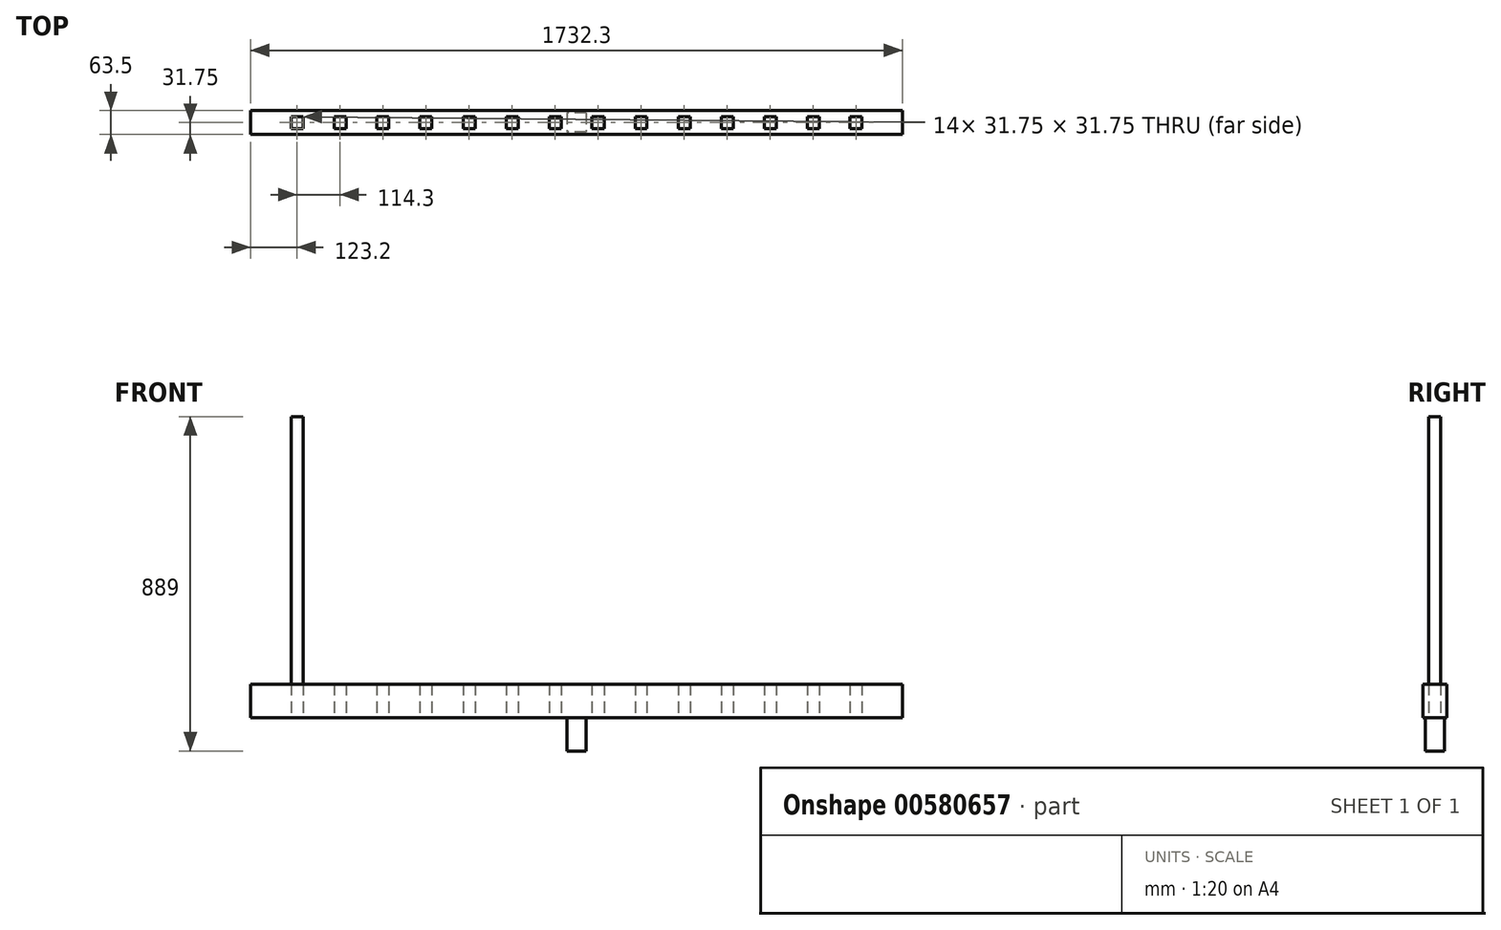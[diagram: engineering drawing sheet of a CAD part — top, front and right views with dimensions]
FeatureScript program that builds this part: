
annotation { "Feature Type Name" : "Feature", "Feature Type Description" : "" }
export const myFeature = defineFeature(function(context is Context, id is Id, definition is map)
    precondition{}
    {
        {
            var Q0;
            Q0=qCreatedBy(makeId("Top.planeOp"),FACE);
            var sketch = newSketch(context, id + "F0", { "sketchPlane" : qUnion([Q0])});
            skLineSegment(sketch, "E0.bottom", {"start": v(866.15, -31.75) * mm, "end": v(-866.15, -31.75) * mm});
            skLineSegment(sketch, "E0.top", {"start": v(866.15, 31.75) * mm, "end": v(-866.15, 31.75) * mm});
            skLineSegment(sketch, "E0.left", {"start": v(866.15, -31.75) * mm, "end": v(866.15, 31.75) * mm});
            skLineSegment(sketch, "E0.right", {"start": v(-866.15, -31.75) * mm, "end": v(-866.15, 31.75) * mm});
            skPoint(sketch, "E0.middle", {"position": v(0, 0) * mm});
            skLineSegment(sketch, "E1.bottom", {"start": v(-41.28, -15.88) * mm, "end": v(-73.03, -15.87) * mm});
            skLineSegment(sketch, "E1.top", {"start": v(-41.28, 15.87) * mm, "end": v(-73.03, 15.88) * mm});
            skLineSegment(sketch, "E1.left", {"start": v(-41.28, -15.87) * mm, "end": v(-41.28, 15.88) * mm});
            skLineSegment(sketch, "E1.right", {"start": v(-73.03, -15.87) * mm, "end": v(-73.03, 15.88) * mm});
            skPoint(sketch, "E1.middle", {"position": v(-57.15, 0) * mm});
            skLineSegment(sketch, "E2.bottom", {"start": v(-155.57, -15.87) * mm, "end": v(-187.32, -15.87) * mm});
            skLineSegment(sketch, "E2.top", {"start": v(-155.58, 15.88) * mm, "end": v(-187.33, 15.88) * mm});
            skLineSegment(sketch, "E2.left", {"start": v(-155.58, -15.87) * mm, "end": v(-155.58, 15.88) * mm});
            skLineSegment(sketch, "E2.right", {"start": v(-187.32, -15.87) * mm, "end": v(-187.32, 15.88) * mm});
            skPoint(sketch, "E2.middle", {"position": v(-171.45, 0) * mm});
            skLineSegment(sketch, "E3.bottom", {"start": v(-269.88, -15.87) * mm, "end": v(-301.63, -15.87) * mm});
            skLineSegment(sketch, "E3.top", {"start": v(-269.88, 15.88) * mm, "end": v(-301.63, 15.88) * mm});
            skLineSegment(sketch, "E3.left", {"start": v(-269.88, -15.87) * mm, "end": v(-269.88, 15.88) * mm});
            skLineSegment(sketch, "E3.right", {"start": v(-301.63, -15.87) * mm, "end": v(-301.63, 15.88) * mm});
            skPoint(sketch, "E3.middle", {"position": v(-285.75, 0) * mm});
            skPoint(sketch, "E3.cornerSnap0", {"position": v(-171.45, -15.87) * mm});
            skLineSegment(sketch, "E4.bottom", {"start": v(-384.18, -15.87) * mm, "end": v(-415.93, -15.87) * mm});
            skLineSegment(sketch, "E4.top", {"start": v(-384.18, 15.87) * mm, "end": v(-415.93, 15.87) * mm});
            skLineSegment(sketch, "E4.left", {"start": v(-384.18, -15.87) * mm, "end": v(-384.18, 15.87) * mm});
            skLineSegment(sketch, "E4.right", {"start": v(-415.93, -15.87) * mm, "end": v(-415.93, 15.87) * mm});
            skPoint(sketch, "E4.middle", {"position": v(-400.05, 0) * mm});
            skPoint(sketch, "E4.cornerSnap0", {"position": v(-285.75, -15.87) * mm});
            skLineSegment(sketch, "E5.bottom", {"start": v(-498.48, -15.87) * mm, "end": v(-530.23, -15.87) * mm});
            skLineSegment(sketch, "E5.top", {"start": v(-498.48, 15.88) * mm, "end": v(-530.23, 15.88) * mm});
            skLineSegment(sketch, "E5.left", {"start": v(-498.48, -15.87) * mm, "end": v(-498.48, 15.87) * mm});
            skLineSegment(sketch, "E5.right", {"start": v(-530.23, -15.88) * mm, "end": v(-530.23, 15.88) * mm});
            skPoint(sketch, "E5.middle", {"position": v(-514.35, 0) * mm});
            skPoint(sketch, "E5.middle.positionSnap0", {"position": v(-415.93, 0) * mm});
            skPoint(sketch, "E5.centerSnap0", {"position": v(-415.93, 0) * mm});
            skLineSegment(sketch, "E6.bottom", {"start": v(-612.77, -15.87) * mm, "end": v(-644.52, -15.87) * mm});
            skLineSegment(sketch, "E6.top", {"start": v(-612.77, 15.88) * mm, "end": v(-644.52, 15.88) * mm});
            skLineSegment(sketch, "E6.left", {"start": v(-612.77, -15.88) * mm, "end": v(-612.77, 15.88) * mm});
            skLineSegment(sketch, "E6.right", {"start": v(-644.52, -15.88) * mm, "end": v(-644.52, 15.87) * mm});
            skPoint(sketch, "E6.middle", {"position": v(-628.65, 0) * mm});
            skLineSegment(sketch, "E7.bottom", {"start": v(-727.07, -15.88) * mm, "end": v(-758.82, -15.88) * mm});
            skLineSegment(sketch, "E7.top", {"start": v(-727.07, 15.87) * mm, "end": v(-758.82, 15.87) * mm});
            skLineSegment(sketch, "E7.left", {"start": v(-727.07, -15.88) * mm, "end": v(-727.07, 15.87) * mm});
            skLineSegment(sketch, "E7.right", {"start": v(-758.82, -15.88) * mm, "end": v(-758.82, 15.87) * mm});
            skPoint(sketch, "E7.middle", {"position": v(-742.95, 0) * mm});
            skLineSegment(sketch, "E8.bottom", {"start": v(73.03, -15.88) * mm, "end": v(41.27, -15.88) * mm});
            skLineSegment(sketch, "E8.top", {"start": v(73.03, 15.87) * mm, "end": v(41.28, 15.87) * mm});
            skLineSegment(sketch, "E8.left", {"start": v(73.03, -15.88) * mm, "end": v(73.03, 15.87) * mm});
            skLineSegment(sketch, "E8.right", {"start": v(41.28, -15.88) * mm, "end": v(41.28, 15.87) * mm});
            skPoint(sketch, "E8.middle", {"position": v(57.15, 0) * mm});
            skLineSegment(sketch, "E9.bottom", {"start": v(187.33, -15.88) * mm, "end": v(155.58, -15.88) * mm});
            skLineSegment(sketch, "E9.top", {"start": v(187.33, 15.87) * mm, "end": v(155.58, 15.87) * mm});
            skLineSegment(sketch, "E9.left", {"start": v(187.33, -15.88) * mm, "end": v(187.33, 15.87) * mm});
            skLineSegment(sketch, "E9.right", {"start": v(155.58, -15.88) * mm, "end": v(155.58, 15.87) * mm});
            skPoint(sketch, "E9.middle", {"position": v(171.45, 0) * mm});
            skLineSegment(sketch, "E10.bottom", {"start": v(301.63, -15.88) * mm, "end": v(269.88, -15.88) * mm});
            skLineSegment(sketch, "E10.top", {"start": v(301.63, 15.87) * mm, "end": v(269.88, 15.87) * mm});
            skLineSegment(sketch, "E10.left", {"start": v(301.63, -15.88) * mm, "end": v(301.63, 15.87) * mm});
            skLineSegment(sketch, "E10.right", {"start": v(269.88, -15.88) * mm, "end": v(269.88, 15.87) * mm});
            skPoint(sketch, "E10.middle", {"position": v(285.75, 0) * mm});
            skLineSegment(sketch, "E11.bottom", {"start": v(415.93, -15.88) * mm, "end": v(384.18, -15.88) * mm});
            skLineSegment(sketch, "E11.top", {"start": v(415.93, 15.87) * mm, "end": v(384.18, 15.87) * mm});
            skLineSegment(sketch, "E11.left", {"start": v(415.93, -15.88) * mm, "end": v(415.93, 15.87) * mm});
            skLineSegment(sketch, "E11.right", {"start": v(384.18, -15.88) * mm, "end": v(384.18, 15.87) * mm});
            skPoint(sketch, "E11.middle", {"position": v(400.05, 0) * mm});
            skLineSegment(sketch, "E12.bottom", {"start": v(530.23, -15.88) * mm, "end": v(498.48, -15.88) * mm});
            skLineSegment(sketch, "E12.top", {"start": v(530.23, 15.87) * mm, "end": v(498.48, 15.87) * mm});
            skLineSegment(sketch, "E12.left", {"start": v(530.23, -15.88) * mm, "end": v(530.23, 15.87) * mm});
            skLineSegment(sketch, "E12.right", {"start": v(498.48, -15.88) * mm, "end": v(498.48, 15.87) * mm});
            skPoint(sketch, "E12.middle", {"position": v(514.35, 0) * mm});
            skLineSegment(sketch, "E13.bottom", {"start": v(644.53, -15.88) * mm, "end": v(612.78, -15.88) * mm});
            skLineSegment(sketch, "E13.top", {"start": v(644.53, 15.87) * mm, "end": v(612.78, 15.87) * mm});
            skLineSegment(sketch, "E13.left", {"start": v(644.53, -15.88) * mm, "end": v(644.53, 15.87) * mm});
            skLineSegment(sketch, "E13.right", {"start": v(612.78, -15.88) * mm, "end": v(612.78, 15.87) * mm});
            skPoint(sketch, "E13.middle", {"position": v(628.65, 0) * mm});
            skLineSegment(sketch, "E14.bottom", {"start": v(758.82, -15.88) * mm, "end": v(727.07, -15.88) * mm});
            skLineSegment(sketch, "E14.top", {"start": v(758.82, 15.87) * mm, "end": v(727.07, 15.87) * mm});
            skLineSegment(sketch, "E14.left", {"start": v(758.82, -15.88) * mm, "end": v(758.82, 15.87) * mm});
            skLineSegment(sketch, "E14.right", {"start": v(727.07, -15.88) * mm, "end": v(727.07, 15.87) * mm});
            skPoint(sketch, "E14.middle", {"position": v(742.95, 0) * mm});
            skSolve(sketch);
        }
        {
            var Q0;
            Q0=makeQuery(id+"F0.imprint","IMPRINT",FACE,{"disambiguationData":[TD([[makeQuery(id+"F0.imprint","IMPRINT",EDGE,{"derivedFrom":sQuery(id+"F0.wireOp",EDGE,"E0.bottom")}),-1.0]])]});
            extrude(context, id + "F1", {"entities" : qUnion([Q0]), "depth" : 88.9 * mm, "offsetDistance" : 25.4 * mm});
        }
        {
            var Q0;
            Q0=makeQuery(id+"F1.opExtrude","CAP_FACE",FACE,{"disambiguationData":[OSD([sQuery(id+"F0.wireOp",EDGE,"E0.bottom"),sQuery(id+"F0.wireOp",EDGE,"E0.top"),sQuery(id+"F0.wireOp",EDGE,"E0.left"),sQuery(id+"F0.wireOp",EDGE,"E0.right"),sQuery(id+"F0.wireOp",EDGE,"E1.bottom"),sQuery(id+"F0.wireOp",EDGE,"E1.top"),sQuery(id+"F0.wireOp",EDGE,"E1.left"),sQuery(id+"F0.wireOp",EDGE,"E1.right"),sQuery(id+"F0.wireOp",EDGE,"E2.bottom"),sQuery(id+"F0.wireOp",EDGE,"E2.top"),sQuery(id+"F0.wireOp",EDGE,"E2.left"),sQuery(id+"F0.wireOp",EDGE,"E2.right"),sQuery(id+"F0.wireOp",EDGE,"E3.bottom"),sQuery(id+"F0.wireOp",EDGE,"E3.top"),sQuery(id+"F0.wireOp",EDGE,"E3.left"),sQuery(id+"F0.wireOp",EDGE,"E3.right"),sQuery(id+"F0.wireOp",EDGE,"E4.bottom"),sQuery(id+"F0.wireOp",EDGE,"E4.top"),sQuery(id+"F0.wireOp",EDGE,"E4.left"),sQuery(id+"F0.wireOp",EDGE,"E4.right"),sQuery(id+"F0.wireOp",EDGE,"E5.bottom"),sQuery(id+"F0.wireOp",EDGE,"E5.top"),sQuery(id+"F0.wireOp",EDGE,"E5.left"),sQuery(id+"F0.wireOp",EDGE,"E5.right"),sQuery(id+"F0.wireOp",EDGE,"E6.bottom"),sQuery(id+"F0.wireOp",EDGE,"E6.top"),sQuery(id+"F0.wireOp",EDGE,"E6.left"),sQuery(id+"F0.wireOp",EDGE,"E6.right"),sQuery(id+"F0.wireOp",EDGE,"E7.bottom"),sQuery(id+"F0.wireOp",EDGE,"E7.top"),sQuery(id+"F0.wireOp",EDGE,"E7.left"),sQuery(id+"F0.wireOp",EDGE,"E7.right"),sQuery(id+"F0.wireOp",EDGE,"E8.bottom"),sQuery(id+"F0.wireOp",EDGE,"E8.top"),sQuery(id+"F0.wireOp",EDGE,"E8.left"),sQuery(id+"F0.wireOp",EDGE,"E8.right"),sQuery(id+"F0.wireOp",EDGE,"E9.bottom"),sQuery(id+"F0.wireOp",EDGE,"E9.top"),sQuery(id+"F0.wireOp",EDGE,"E9.left"),sQuery(id+"F0.wireOp",EDGE,"E9.right"),sQuery(id+"F0.wireOp",EDGE,"E10.bottom"),sQuery(id+"F0.wireOp",EDGE,"E10.top"),sQuery(id+"F0.wireOp",EDGE,"E10.left"),sQuery(id+"F0.wireOp",EDGE,"E10.right"),sQuery(id+"F0.wireOp",EDGE,"E11.bottom"),sQuery(id+"F0.wireOp",EDGE,"E11.top"),sQuery(id+"F0.wireOp",EDGE,"E11.left"),sQuery(id+"F0.wireOp",EDGE,"E11.right"),sQuery(id+"F0.wireOp",EDGE,"E12.bottom"),sQuery(id+"F0.wireOp",EDGE,"E12.top"),sQuery(id+"F0.wireOp",EDGE,"E12.left"),sQuery(id+"F0.wireOp",EDGE,"E12.right"),sQuery(id+"F0.wireOp",EDGE,"E13.bottom"),sQuery(id+"F0.wireOp",EDGE,"E13.top"),sQuery(id+"F0.wireOp",EDGE,"E13.left"),sQuery(id+"F0.wireOp",EDGE,"E13.right"),sQuery(id+"F0.wireOp",EDGE,"E14.bottom"),sQuery(id+"F0.wireOp",EDGE,"E14.top"),sQuery(id+"F0.wireOp",EDGE,"E14.left"),sQuery(id+"F0.wireOp",EDGE,"E14.right")])],"isStart":false});
            var sketch = newSketch(context, id + "F2", { "sketchPlane" : qUnion([Q0])});
            skLineSegment(sketch, "E15.bottom", {"start": v(-758.82, 15.87) * mm, "end": v(-727.07, 15.87) * mm});
            skLineSegment(sketch, "E15.top", {"start": v(-758.82, -15.88) * mm, "end": v(-727.07, -15.88) * mm});
            skLineSegment(sketch, "E15.left", {"start": v(-758.82, 15.87) * mm, "end": v(-758.82, -15.88) * mm});
            skLineSegment(sketch, "E15.right", {"start": v(-727.07, 15.87) * mm, "end": v(-727.07, -15.88) * mm});
            skSolve(sketch);
        }
        {
            var Q0;
            Q0=makeQuery(id+"F1.opExtrude","CAP_FACE",FACE,{"disambiguationData":[OSD([sQuery(id+"F0.wireOp",EDGE,"E0.bottom"),sQuery(id+"F0.wireOp",EDGE,"E0.top"),sQuery(id+"F0.wireOp",EDGE,"E0.left"),sQuery(id+"F0.wireOp",EDGE,"E0.right"),sQuery(id+"F0.wireOp",EDGE,"E1.bottom"),sQuery(id+"F0.wireOp",EDGE,"E1.top"),sQuery(id+"F0.wireOp",EDGE,"E1.left"),sQuery(id+"F0.wireOp",EDGE,"E1.right"),sQuery(id+"F0.wireOp",EDGE,"E2.bottom"),sQuery(id+"F0.wireOp",EDGE,"E2.top"),sQuery(id+"F0.wireOp",EDGE,"E2.left"),sQuery(id+"F0.wireOp",EDGE,"E2.right"),sQuery(id+"F0.wireOp",EDGE,"E3.bottom"),sQuery(id+"F0.wireOp",EDGE,"E3.top"),sQuery(id+"F0.wireOp",EDGE,"E3.left"),sQuery(id+"F0.wireOp",EDGE,"E3.right"),sQuery(id+"F0.wireOp",EDGE,"E4.bottom"),sQuery(id+"F0.wireOp",EDGE,"E4.top"),sQuery(id+"F0.wireOp",EDGE,"E4.left"),sQuery(id+"F0.wireOp",EDGE,"E4.right"),sQuery(id+"F0.wireOp",EDGE,"E5.bottom"),sQuery(id+"F0.wireOp",EDGE,"E5.top"),sQuery(id+"F0.wireOp",EDGE,"E5.left"),sQuery(id+"F0.wireOp",EDGE,"E5.right"),sQuery(id+"F0.wireOp",EDGE,"E6.bottom"),sQuery(id+"F0.wireOp",EDGE,"E6.top"),sQuery(id+"F0.wireOp",EDGE,"E6.left"),sQuery(id+"F0.wireOp",EDGE,"E6.right"),sQuery(id+"F0.wireOp",EDGE,"E7.bottom"),sQuery(id+"F0.wireOp",EDGE,"E7.top"),sQuery(id+"F0.wireOp",EDGE,"E7.left"),sQuery(id+"F0.wireOp",EDGE,"E7.right"),sQuery(id+"F0.wireOp",EDGE,"E8.bottom"),sQuery(id+"F0.wireOp",EDGE,"E8.top"),sQuery(id+"F0.wireOp",EDGE,"E8.left"),sQuery(id+"F0.wireOp",EDGE,"E8.right"),sQuery(id+"F0.wireOp",EDGE,"E9.bottom"),sQuery(id+"F0.wireOp",EDGE,"E9.top"),sQuery(id+"F0.wireOp",EDGE,"E9.left"),sQuery(id+"F0.wireOp",EDGE,"E9.right"),sQuery(id+"F0.wireOp",EDGE,"E10.bottom"),sQuery(id+"F0.wireOp",EDGE,"E10.top"),sQuery(id+"F0.wireOp",EDGE,"E10.left"),sQuery(id+"F0.wireOp",EDGE,"E10.right"),sQuery(id+"F0.wireOp",EDGE,"E11.bottom"),sQuery(id+"F0.wireOp",EDGE,"E11.top"),sQuery(id+"F0.wireOp",EDGE,"E11.left"),sQuery(id+"F0.wireOp",EDGE,"E11.right"),sQuery(id+"F0.wireOp",EDGE,"E12.bottom"),sQuery(id+"F0.wireOp",EDGE,"E12.top"),sQuery(id+"F0.wireOp",EDGE,"E12.left"),sQuery(id+"F0.wireOp",EDGE,"E12.right"),sQuery(id+"F0.wireOp",EDGE,"E13.bottom"),sQuery(id+"F0.wireOp",EDGE,"E13.top"),sQuery(id+"F0.wireOp",EDGE,"E13.left"),sQuery(id+"F0.wireOp",EDGE,"E13.right"),sQuery(id+"F0.wireOp",EDGE,"E14.bottom"),sQuery(id+"F0.wireOp",EDGE,"E14.top"),sQuery(id+"F0.wireOp",EDGE,"E14.left"),sQuery(id+"F0.wireOp",EDGE,"E14.right")])],"isStart":true});
            var sketch = newSketch(context, id + "F3", { "sketchPlane" : qUnion([Q0])});
            skLineSegment(sketch, "E16.bottom", {"start": v(25.4, -25.4) * mm, "end": v(-25.4, -25.4) * mm});
            skLineSegment(sketch, "E16.top", {"start": v(25.4, 25.4) * mm, "end": v(-25.4, 25.4) * mm});
            skLineSegment(sketch, "E16.left", {"start": v(25.4, -25.4) * mm, "end": v(25.4, 25.4) * mm});
            skLineSegment(sketch, "E16.right", {"start": v(-25.4, -25.4) * mm, "end": v(-25.4, 25.4) * mm});
            skPoint(sketch, "E16.middle", {"position": v(0, 0) * mm});
            skSolve(sketch);
        }
        {
            var Q0;
            Q0=makeQuery(id+"F3.imprint","IMPRINT",FACE,{"disambiguationData":[TD([[makeQuery(id+"F3.imprint","IMPRINT",EDGE,{"derivedFrom":sQuery(id+"F3.wireOp",EDGE,"E16.bottom")}),-1.0]])]});
            extrude(context, id + "F4", {"entities" : qUnion([Q0]), "operationType" : NewBodyOperationType.ADD, "depth" : 88.9 * mm, "offsetDistance" : 25.4 * mm});
        }
        {
            var Q0;
            Q0=makeQuery(id+"F2.imprint","IMPRINT",FACE,{"disambiguationData":[TD([[makeQuery(id+"F2.imprint","IMPRINT",EDGE,{"derivedFrom":sQuery(id+"F2.wireOp",EDGE,"E15.bottom")}),1.0]])]});
            extrude(context, id + "F5", {"entities" : qUnion([Q0]), "depth" : 711.2 * mm, "offsetDistance" : 25.4 * mm});
        }
    });
